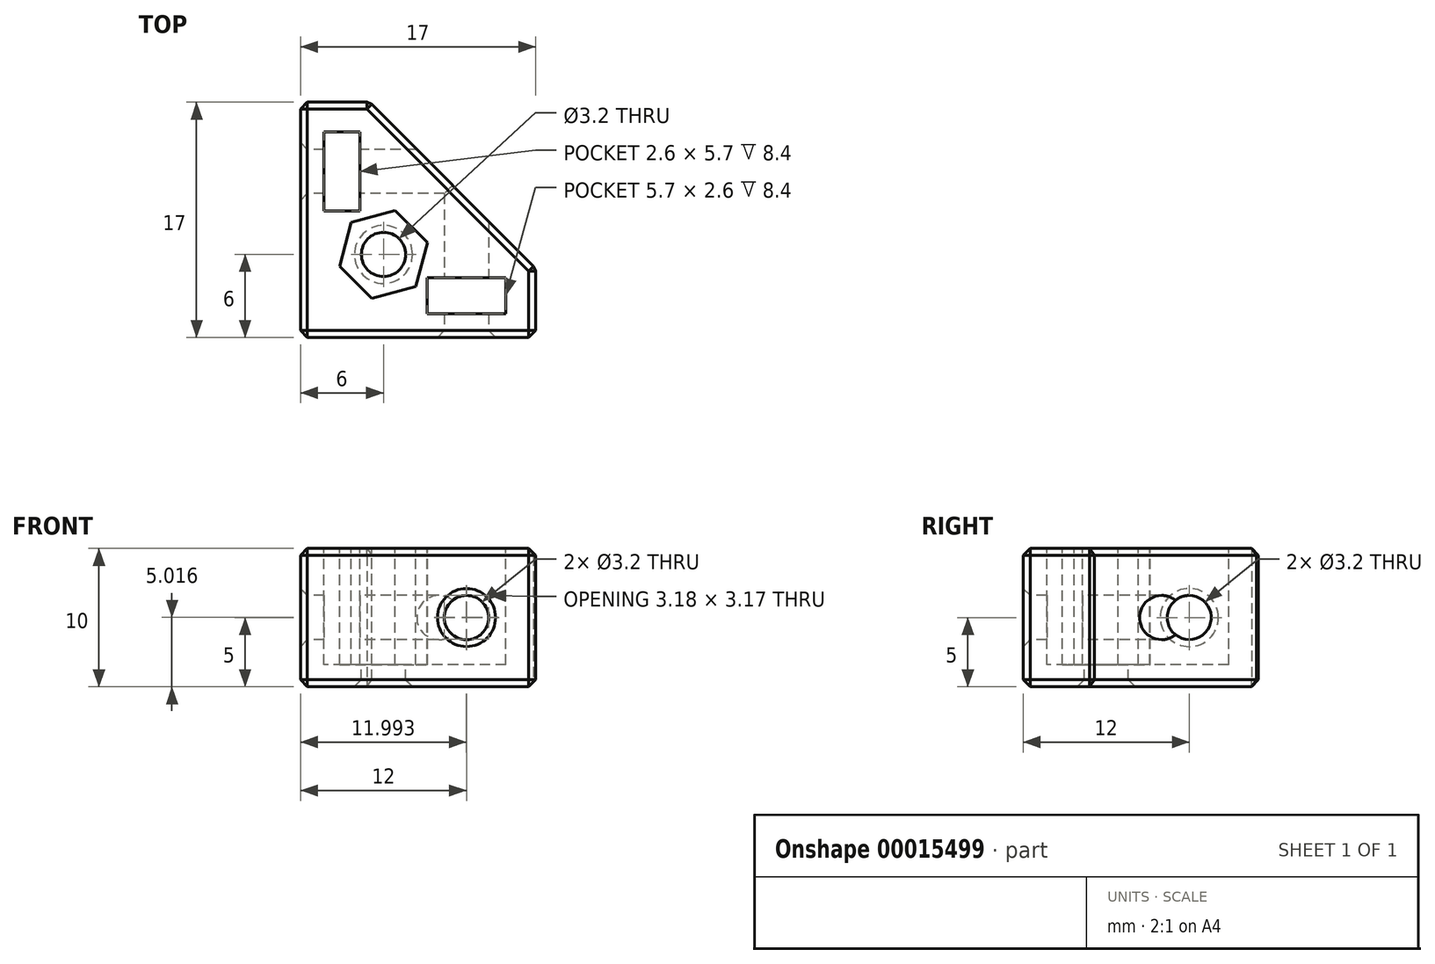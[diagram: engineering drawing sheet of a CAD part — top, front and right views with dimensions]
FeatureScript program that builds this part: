
annotation { "Feature Type Name" : "Feature", "Feature Type Description" : "" }
export const myFeature = defineFeature(function(context is Context, id is Id, definition is map)
    precondition{}
    {
        {
            var Q0;
            Q0=qCreatedBy(makeId("Top.planeOp"),FACE);
            var sketch = newSketch(context, id + "F0", { "sketchPlane" : qUnion([Q0])});
            skLineSegment(sketch, "E0", {"start": v(0, 0) * mm, "end": v(0, 17) * mm});
            skLineSegment(sketch, "E1", {"start": v(0, 17) * mm, "end": v(17, 0) * mm, "construction": true});
            skLineSegment(sketch, "E2", {"start": v(17, 0) * mm, "end": v(0, 0) * mm});
            skLineSegment(sketch, "E3", {"start": v(17, 0) * mm, "end": v(17, 5) * mm});
            skLineSegment(sketch, "E4", {"start": v(17, 5) * mm, "end": v(5, 17) * mm});
            skLineSegment(sketch, "E5", {"start": v(5, 17) * mm, "end": v(0, 17) * mm});
            skSolve(sketch);
        }
        {
            var Q0;
            Q0=makeQuery(id+"F0.imprint","IMPRINT",FACE,{"disambiguationData":[TD([[makeQuery(id+"F0.imprint","IMPRINT",EDGE,{"derivedFrom":sQuery(id+"F0.wireOp",EDGE,"E0")}),-1.0]])]});
            extrude(context, id + "F1", {"entities" : qUnion([Q0]), "depth" : 5 * mm, "hasSecondDirection" : true, "secondDirectionOppositeDirection" : true, "secondDirectionDepth" : 5 * mm});
        }
        {
            var Q0;
            Q0=qCreatedBy(makeId("Front.planeOp"),FACE);
            var sketch = newSketch(context, id + "F2", { "sketchPlane" : qUnion([Q0])});
            skPoint(sketch, "E6", {"position": v(12, 0) * mm});
            skLineSegment(sketch, "E7", {"start": v(0, 0) * mm, "end": v(12, 0) * mm, "construction": true});
            skSolve(sketch);
        }
        {
            var Q0;
            Q0=qCreatedBy(makeId("Right.planeOp"),FACE);
            var sketch = newSketch(context, id + "F3", { "sketchPlane" : qUnion([Q0])});
            skPoint(sketch, "E8", {"position": v(12, 0) * mm});
            skLineSegment(sketch, "E9", {"start": v(0, 0) * mm, "end": v(12, 0) * mm, "construction": true});
            skSolve(sketch);
        }
        {
            var Q0;
            Q0=qCreatedBy(makeId("Top.planeOp"),FACE);
            var sketch = newSketch(context, id + "F4", { "sketchPlane" : qUnion([Q0])});
            skPoint(sketch, "E10", {"position": v(6, 6) * mm});
            skSolve(sketch);
        }
        {
            var Q0;
            Q0=sQuery(id+"F2.wireOp",VERTEX,"E6");
            var Q1;
            Q1=sQuery(id+"F4.wireOp",VERTEX,"E10");
            var Q2;
            Q2=makeQuery(id+"F1.opExtrude","SWEPT_BODY",BODY,{"disambiguationData":[OSD([sQuery(id+"F0.wireOp",EDGE,"E0"),sQuery(id+"F0.wireOp",EDGE,"E1"),sQuery(id+"F0.wireOp",EDGE,"E2")])]});
            hole(context, id + "F5", {"style" : HoleStyle.SIMPLE, "holeDiameter" : 3.2 * mm, "endStyle" : HoleEndStyle.THROUGH, "locations" : qUnion([Q0, Q1]), "scope" : qUnion([Q2])});
        }
        {
            var Q0;
            Q0=sQuery(id+"F3.wireOp",VERTEX,"E8");
            var Q1;
            Q1=sQuery(id+"F4.wireOp",VERTEX,"E10");
            var Q2;
            Q2=makeQuery(id+"F1.opExtrude","SWEPT_BODY",BODY,{"disambiguationData":[OSD([sQuery(id+"F0.wireOp",EDGE,"E0"),sQuery(id+"F0.wireOp",EDGE,"E1"),sQuery(id+"F0.wireOp",EDGE,"E2")])]});
            hole(context, id + "F6", {"style" : HoleStyle.SIMPLE, "holeDiameter" : 3.2 * mm, "endStyle" : HoleEndStyle.THROUGH, "oppositeDirection" : true, "locations" : qUnion([Q0, Q1]), "scope" : qUnion([Q2])});
        }
        {
            var Q0;
            Q0=makeQuery(id+"F1.opExtrude","CAP_FACE",FACE,{"disambiguationData":[OSD([sQuery(id+"F0.wireOp",EDGE,"E0"),sQuery(id+"F0.wireOp",EDGE,"E2"),sQuery(id+"F0.wireOp",EDGE,"E3"),sQuery(id+"F0.wireOp",EDGE,"E4"),sQuery(id+"F0.wireOp",EDGE,"E5")])],"isStart":false});
            var sketch = newSketch(context, id + "F7", { "sketchPlane" : qUnion([Q0])});
            skLineSegment(sketch, "E11", {"start": v(3.67, 8.33) * mm, "end": v(2.82, 5.15) * mm});
            skLineSegment(sketch, "E12", {"start": v(2.82, 5.15) * mm, "end": v(5.15, 2.82) * mm});
            skLineSegment(sketch, "E13", {"start": v(5.15, 2.82) * mm, "end": v(8.33, 3.67) * mm});
            skLineSegment(sketch, "E14", {"start": v(8.33, 3.67) * mm, "end": v(9.18, 6.85) * mm});
            skLineSegment(sketch, "E15", {"start": v(9.18, 6.85) * mm, "end": v(6.85, 9.18) * mm});
            skLineSegment(sketch, "E16", {"start": v(6.85, 9.18) * mm, "end": v(3.67, 8.33) * mm});
            skCircle(sketch, "E17", {"center": v(6, 6) * mm, "radius": 2.85 * mm, "construction": true});
            skLineSegment(sketch, "E18.rect.bottom", {"start": v(14.85, 4.3) * mm, "end": v(9.15, 4.3) * mm});
            skLineSegment(sketch, "E18.rect.top", {"start": v(14.85, 1.7) * mm, "end": v(9.15, 1.7) * mm});
            skLineSegment(sketch, "E18.rect.left", {"start": v(14.85, 4.3) * mm, "end": v(14.85, 1.7) * mm});
            skLineSegment(sketch, "E18.rect.right", {"start": v(9.15, 4.3) * mm, "end": v(9.15, 1.7) * mm});
            skPoint(sketch, "E18.rect.middle", {"position": v(12, 3) * mm});
            skLineSegment(sketch, "E19.rect.bottom", {"start": v(4.3, 14.85) * mm, "end": v(1.7, 14.85) * mm});
            skLineSegment(sketch, "E19.rect.top", {"start": v(4.3, 9.15) * mm, "end": v(1.7, 9.15) * mm});
            skLineSegment(sketch, "E19.rect.left", {"start": v(4.3, 14.85) * mm, "end": v(4.3, 9.15) * mm});
            skLineSegment(sketch, "E19.rect.right", {"start": v(1.7, 14.85) * mm, "end": v(1.7, 9.15) * mm});
            skPoint(sketch, "E19.rect.middle", {"position": v(3, 12) * mm});
            skLineSegment(sketch, "E20", {"start": v(3, 12) * mm, "end": v(0, 12) * mm, "construction": true});
            skLineSegment(sketch, "E21", {"start": v(12, 3) * mm, "end": v(12, 0) * mm, "construction": true});
            skSolve(sketch);
        }
        {
            var Q0;
            Q0 = qSketchRegion(id + "F7", true);
            extrude(context, id + "F8", {"entities" : qUnion([Q0]), "operationType" : NewBodyOperationType.REMOVE, "oppositeDirection" : true, "depth" : (5 + 3.4) * mm});
        }
        {
            var Q0;
            Q0=makeQuery(id+"F1.opExtrude","SWEPT_FACE",FACE,{"disambiguationData":[OSD([sQuery(id+"F0.wireOp",EDGE,"E2")])]});
            var Q1;
            Q1=makeQuery(id+"F1.opExtrude","SWEPT_FACE",FACE,{"disambiguationData":[OSD([sQuery(id+"F0.wireOp",EDGE,"E0")])]});
            var Q2;
            Q2=makeQuery(id+"F1.opExtrude","CAP_FACE",FACE,{"disambiguationData":[OSD([sQuery(id+"F0.wireOp",EDGE,"E0"),sQuery(id+"F0.wireOp",EDGE,"E2"),sQuery(id+"F0.wireOp",EDGE,"E3"),sQuery(id+"F0.wireOp",EDGE,"E4"),sQuery(id+"F0.wireOp",EDGE,"E5")])],"isStart":true});
            var Q3;
            Q3=makeQuery(id+"F1.opExtrude","SWEPT_FACE",FACE,{"disambiguationData":[OSD([sQuery(id+"F0.wireOp",EDGE,"E3")])]});
            var Q4;
            Q4=makeQuery(id+"F1.opExtrude","SWEPT_FACE",FACE,{"disambiguationData":[OSD([sQuery(id+"F0.wireOp",EDGE,"E5")])]});
            var Q5;
            Q5=makeQuery(id+"F1.opExtrude","CAP_EDGE",EDGE,{"disambiguationData":[OSD([sQuery(id+"F0.wireOp",EDGE,"E4")])],"isStart":false});
            chamfer(context, id + "F9", {"entities" : qUnion([Q0, Q1, Q2, Q3, Q4, Q5]), "width" : .5 * mm, "tangentPropagation" : true});
        }
    });
